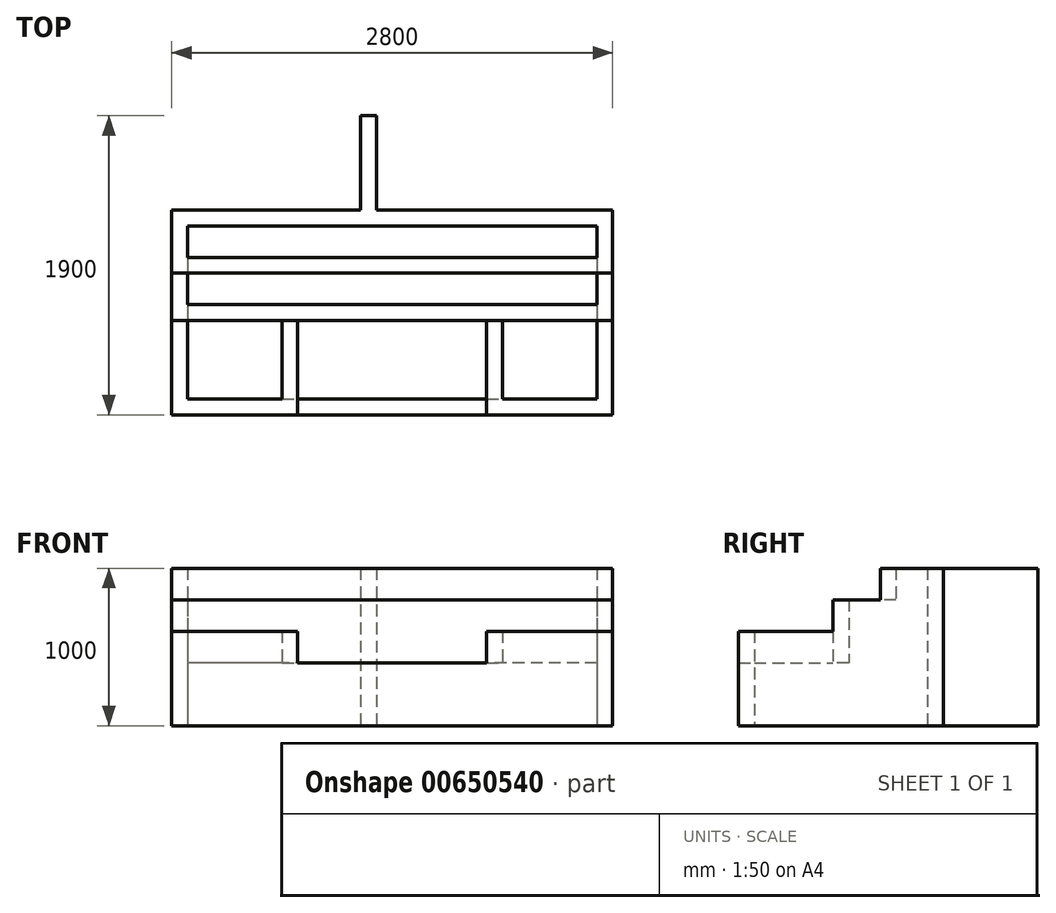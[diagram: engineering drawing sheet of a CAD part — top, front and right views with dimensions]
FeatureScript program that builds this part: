
annotation { "Feature Type Name" : "Feature", "Feature Type Description" : "" }
export const myFeature = defineFeature(function(context is Context, id is Id, definition is map)
    precondition{}
    {
        {
            var Q0;
            Q0=qCreatedBy(makeId("Top.planeOp"),FACE);
            var sketch = newSketch(context, id + "F0", { "sketchPlane" : qUnion([Q0])});
            skLineSegment(sketch, "E0.bottom", {"start": v(0, 0) * mm, "end": v(-2800, 0) * mm});
            skLineSegment(sketch, "E0.top", {"start": v(0, 1300) * mm, "end": v(-2800, 1300) * mm});
            skLineSegment(sketch, "E0.left", {"start": v(0, 0) * mm, "end": v(0, 1300) * mm});
            skLineSegment(sketch, "E0.right", {"start": v(-2800, 0) * mm, "end": v(-2800, 1300) * mm});
            skLineSegment(sketch, "E1.bottom", {"start": v(-2700, 1200) * mm, "end": v(-100, 1200) * mm});
            skLineSegment(sketch, "E1.top", {"start": v(-2700, 100) * mm, "end": v(-100, 100) * mm});
            skLineSegment(sketch, "E1.left", {"start": v(-2700, 1200) * mm, "end": v(-2700, 100) * mm});
            skLineSegment(sketch, "E1.right", {"start": v(-100, 1200) * mm, "end": v(-100, 100) * mm});
            skSolve(sketch);
        }
        {
            var Q0;
            Q0=makeQuery(id+"F0.imprint","IMPRINT",FACE,{"disambiguationData":[TD([[makeQuery(id+"F0.imprint","IMPRINT",EDGE,{"derivedFrom":sQuery(id+"F0.wireOp",EDGE,"E0.bottom")}),-1.0]])]});
            extrude(context, id + "F1", {"entities" : qUnion([Q0]), "depth" : 400 * mm, "offsetDistance" : 25 * mm});
        }
        {
            var Q0;
            Q0=makeQuery(id+"F1.opExtrude","CAP_FACE",FACE,{"disambiguationData":[OSD([sQuery(id+"F0.wireOp",EDGE,"E0.bottom"),sQuery(id+"F0.wireOp",EDGE,"E0.top"),sQuery(id+"F0.wireOp",EDGE,"E0.left"),sQuery(id+"F0.wireOp",EDGE,"E0.right"),sQuery(id+"F0.wireOp",EDGE,"E1.bottom"),sQuery(id+"F0.wireOp",EDGE,"E1.top"),sQuery(id+"F0.wireOp",EDGE,"E1.left"),sQuery(id+"F0.wireOp",EDGE,"E1.right")])],"isStart":false});
            var sketch = newSketch(context, id + "F2", { "sketchPlane" : qUnion([Q0])});
            skLineSegment(sketch, "E2.bottom", {"start": v(0, 600) * mm, "end": v(-2800, 600) * mm});
            skLineSegment(sketch, "E2.top", {"start": v(0, 1300) * mm, "end": v(-2800, 1300) * mm});
            skLineSegment(sketch, "E2.left", {"start": v(0, 600) * mm, "end": v(0, 1300) * mm});
            skLineSegment(sketch, "E2.right", {"start": v(-2800, 600) * mm, "end": v(-2800, 1300) * mm});
            skLineSegment(sketch, "E3.bottom", {"start": v(-100, 700) * mm, "end": v(-2700, 700) * mm});
            skLineSegment(sketch, "E3.top", {"start": v(-100, 1200) * mm, "end": v(-2700, 1200) * mm});
            skLineSegment(sketch, "E3.left", {"start": v(-100, 700) * mm, "end": v(-100, 1200) * mm});
            skLineSegment(sketch, "E3.right", {"start": v(-2700, 700) * mm, "end": v(-2700, 1200) * mm});
            skSolve(sketch);
        }
        {
            var Q0;
            Q0 = qSketchRegion(id + "F2", true);
            extrude(context, id + "F3", {"entities" : qUnion([Q0]), "operationType" : NewBodyOperationType.ADD, "depth" : 400 * mm, "offsetDistance" : 25 * mm});
        }
        {
            var Q0;
            Q0=makeQuery(id+"F3.opExtrude","CAP_FACE",FACE,{"disambiguationData":[OSD([sQuery(id+"F2.wireOp",EDGE,"E2.bottom"),sQuery(id+"F2.wireOp",EDGE,"E2.top"),sQuery(id+"F2.wireOp",EDGE,"E2.left"),sQuery(id+"F2.wireOp",EDGE,"E2.right"),sQuery(id+"F2.wireOp",EDGE,"E3.bottom"),sQuery(id+"F2.wireOp",EDGE,"E3.top"),sQuery(id+"F2.wireOp",EDGE,"E3.left"),sQuery(id+"F2.wireOp",EDGE,"E3.right")])],"isStart":false});
            var sketch = newSketch(context, id + "F4", { "sketchPlane" : qUnion([Q0])});
            skLineSegment(sketch, "E4.bottom", {"start": v(0, 900) * mm, "end": v(-2800, 900) * mm});
            skLineSegment(sketch, "E4.top", {"start": v(0, 1300) * mm, "end": v(-2800, 1300) * mm});
            skLineSegment(sketch, "E4.left", {"start": v(0, 900) * mm, "end": v(0, 1300) * mm});
            skLineSegment(sketch, "E4.right", {"start": v(-2800, 900) * mm, "end": v(-2800, 1300) * mm});
            skLineSegment(sketch, "E5.bottom", {"start": v(-100, 1000) * mm, "end": v(-2700, 1000) * mm});
            skLineSegment(sketch, "E5.top", {"start": v(-100, 1200) * mm, "end": v(-2700, 1200) * mm});
            skLineSegment(sketch, "E5.left", {"start": v(-100, 1000) * mm, "end": v(-100, 1200) * mm});
            skLineSegment(sketch, "E5.right", {"start": v(-2700, 1000) * mm, "end": v(-2700, 1200) * mm});
            skSolve(sketch);
        }
        {
            var Q0;
            Q0 = qSketchRegion(id + "F4", true);
            extrude(context, id + "F5", {"entities" : qUnion([Q0]), "operationType" : NewBodyOperationType.ADD, "depth" : 200 * mm, "offsetDistance" : 25 * mm});
        }
        {
            var Q0;
            Q0=qCreatedBy(makeId("Top.planeOp"),FACE);
            var sketch = newSketch(context, id + "F6", { "sketchPlane" : qUnion([Q0])});
            skLineSegment(sketch, "E6.bottom", {"start": v(-1500, 1300) * mm, "end": v(-1600, 1300) * mm});
            skLineSegment(sketch, "E6.top", {"start": v(-1500, 1900) * mm, "end": v(-1600, 1900) * mm});
            skLineSegment(sketch, "E6.left", {"start": v(-1500, 1300) * mm, "end": v(-1500, 1900) * mm});
            skLineSegment(sketch, "E6.right", {"start": v(-1600, 1300) * mm, "end": v(-1600, 1900) * mm});
            skSolve(sketch);
        }
        {
            var Q0;
            Q0 = qSketchRegion(id + "F6", true);
            extrude(context, id + "F7", {"entities" : qUnion([Q0]), "operationType" : NewBodyOperationType.ADD, "depth" : 1000 * mm, "offsetDistance" : 25 * mm});
        }
        {
            var Q0;
            Q0=makeQuery(id+"F1.opExtrude","CAP_FACE",FACE,{"disambiguationData":[OSD([sQuery(id+"F0.wireOp",EDGE,"E0.bottom"),sQuery(id+"F0.wireOp",EDGE,"E0.top"),sQuery(id+"F0.wireOp",EDGE,"E0.left"),sQuery(id+"F0.wireOp",EDGE,"E0.right"),sQuery(id+"F0.wireOp",EDGE,"E1.bottom"),sQuery(id+"F0.wireOp",EDGE,"E1.top"),sQuery(id+"F0.wireOp",EDGE,"E1.left"),sQuery(id+"F0.wireOp",EDGE,"E1.right")])],"isStart":false});
            var sketch = newSketch(context, id + "F8", { "sketchPlane" : qUnion([Q0])});
            skLineSegment(sketch, "E7.bottom", {"start": v(-2800, 0) * mm, "end": v(-2000, 0) * mm});
            skLineSegment(sketch, "E7.left", {"start": v(-2800, 0) * mm, "end": v(-2800, 600) * mm});
            skLineSegment(sketch, "E7.right", {"start": v(-2000, 0) * mm, "end": v(-2000, 600) * mm});
            skLineSegment(sketch, "E8.bottom", {"start": v(-2700, 100) * mm, "end": v(-2100, 100) * mm});
            skPoint(sketch, "E9.oppositeSnap0", {"position": v(-50, 600) * mm});
            skLineSegment(sketch, "E9.bottom", {"start": v(0, 0) * mm, "end": v(-800, 0) * mm});
            skLineSegment(sketch, "E9.top", {"start": v(0, 600) * mm, "end": v(-800, 600) * mm});
            skLineSegment(sketch, "E9.left", {"start": v(0, 0) * mm, "end": v(0, 600) * mm});
            skLineSegment(sketch, "E9.right", {"start": v(-800, 0) * mm, "end": v(-800, 600) * mm});
            skLineSegment(sketch, "E10.bottom", {"start": v(0, 0) * mm, "end": v(-700, 0) * mm});
            skLineSegment(sketch, "E10.left", {"start": v(0, 0) * mm, "end": v(0, 500) * mm});
            skLineSegment(sketch, "E11", {"start": v(-2800, 600) * mm, "end": v(-2000, 600) * mm});
            skLineSegment(sketch, "E12", {"start": v(-2700, 100) * mm, "end": v(-2700, 600) * mm});
            skLineSegment(sketch, "E13", {"start": v(-2700, 600) * mm, "end": v(-2100, 600) * mm});
            skLineSegment(sketch, "E14", {"start": v(-2100, 600) * mm, "end": v(-2100, 100) * mm});
            skLineSegment(sketch, "E15", {"start": v(-800, 600) * mm, "end": v(0, 600) * mm});
            skLineSegment(sketch, "E16", {"start": v(-700, 0) * mm, "end": v(-700, 600) * mm});
            skLineSegment(sketch, "E17", {"start": v(-100, 600) * mm, "end": v(-100, 0) * mm});
            skSolve(sketch);
        }
        {
            var Q0;
            {var subQ0=sQuery(id+"F8.wireOp",EDGE,"E15");var subQ1=sQuery(id+"F8.wireOp",EDGE,"E9.right");var subQ2=makeQuery(id+"F8.imprint","INTERSECT",VERTEX,{"derivedFrom":[subQ1,subQ0]});Q0=makeQuery(id+"F8.imprint","IMPRINT",FACE,{"disambiguationData":[TD([[makeQuery(id+"F8.imprint","IMPRINT",EDGE,{"disambiguationData":[TD([[subQ2,1.0]])],"derivedFrom":subQ1}),-1.0]])]});}
            var Q1;
            {var subQ0=sQuery(id+"F8.wireOp",EDGE,"E9.bottom");Q1=makeQuery(id+"F8.imprint","IMPRINT",FACE,{"disambiguationData":[TD([[makeQuery(id+"F8.imprint","IMPRINT",EDGE,{"derivedFrom":subQ0}),-1.0]])]});}
            var Q2;
            {var subQ3=sQuery(id+"F8.wireOp",EDGE,"E17");var subQ5=makeQuery(id+"F1.opExtrude","CAP_EDGE",EDGE,{"disambiguationData":[OSD([sQuery(id+"F0.wireOp",EDGE,"E1.top")])],"isStart":false});var subQ7=makeQuery(id+"F8.imprint","INTERSECT",VERTEX,{"derivedFrom":[subQ5,subQ3]});Q2=makeQuery(id+"F8.imprint","IMPRINT",FACE,{"disambiguationData":[TD([[makeQuery(id+"F8.imprint","IMPRINT",EDGE,{"disambiguationData":[TD([[subQ7,-1.0]])],"derivedFrom":subQ3}),-1.0]])]});}
            var Q3;
            {var subQ1=sQuery(id+"F8.wireOp",EDGE,"E9.left");Q3=makeQuery(id+"F8.imprint","IMPRINT",FACE,{"disambiguationData":[TD([[makeQuery(id+"F8.imprint","IMPRINT",EDGE,{"derivedFrom":subQ1}),1.0]])]});}
            var Q4;
            {var subQ5=sQuery(id+"F8.wireOp",EDGE,"E14");Q4=makeQuery(id+"F8.imprint","IMPRINT",FACE,{"disambiguationData":[TD([[makeQuery(id+"F8.imprint","IMPRINT",EDGE,{"derivedFrom":subQ5}),1.0]])]});}
            var Q5;
            {var subQ4=sQuery(id+"F8.wireOp",EDGE,"E7.bottom");Q5=makeQuery(id+"F8.imprint","IMPRINT",FACE,{"disambiguationData":[TD([[makeQuery(id+"F8.imprint","IMPRINT",EDGE,{"derivedFrom":subQ4}),-1.0]])]});}
            extrude(context, id + "F9", {"entities" : qUnion([Q0, Q1, Q2, Q3, Q4, Q5]), "operationType" : NewBodyOperationType.ADD, "depth" : 200 * mm, "offsetDistance" : 25 * mm});
        }
    });
